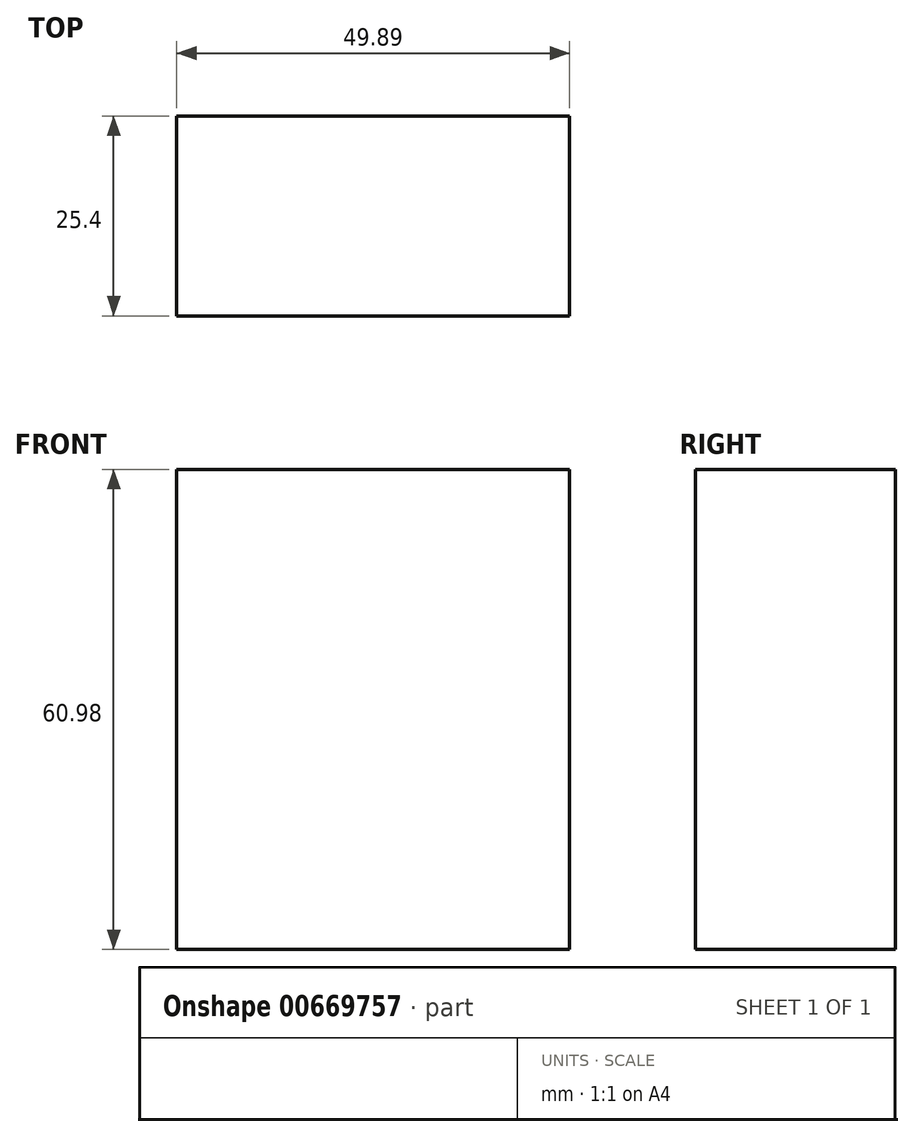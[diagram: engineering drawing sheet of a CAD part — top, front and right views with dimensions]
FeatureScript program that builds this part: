
annotation { "Feature Type Name" : "Feature", "Feature Type Description" : "" }
export const myFeature = defineFeature(function(context is Context, id is Id, definition is map)
    precondition{}
    {
        {
            var Q0;
            Q0=qCreatedBy(makeId("Front.planeOp"),FACE);
            var sketch = newSketch(context, id + "F0", { "sketchPlane" : qUnion([Q0])});
            skLineSegment(sketch, "E0", {"start": v(0, 0) * mm, "end": v(0, 60.98) * mm});
            skLineSegment(sketch, "E1", {"start": v(0, 60.98) * mm, "end": v(49.89, 60.98) * mm});
            skLineSegment(sketch, "E2", {"start": v(49.89, 60.98) * mm, "end": v(49.89, 0) * mm});
            skLineSegment(sketch, "E3", {"start": v(49.89, 0) * mm, "end": v(0, 0) * mm});
            skSolve(sketch);
        }
        {
            var Q0;
            Q0=makeQuery(id+"F0.imprint","IMPRINT",FACE,{"disambiguationData":[TD([[makeQuery(id+"F0.imprint","IMPRINT",EDGE,{"derivedFrom":sQuery(id+"F0.wireOp",EDGE,"E0")}),-1.0]])]});
            extrude(context, id + "F1", {"entities" : qUnion([Q0]), "depth" : 25.4 * mm, "offsetDistance" : 25.4 * mm});
        }
    });
